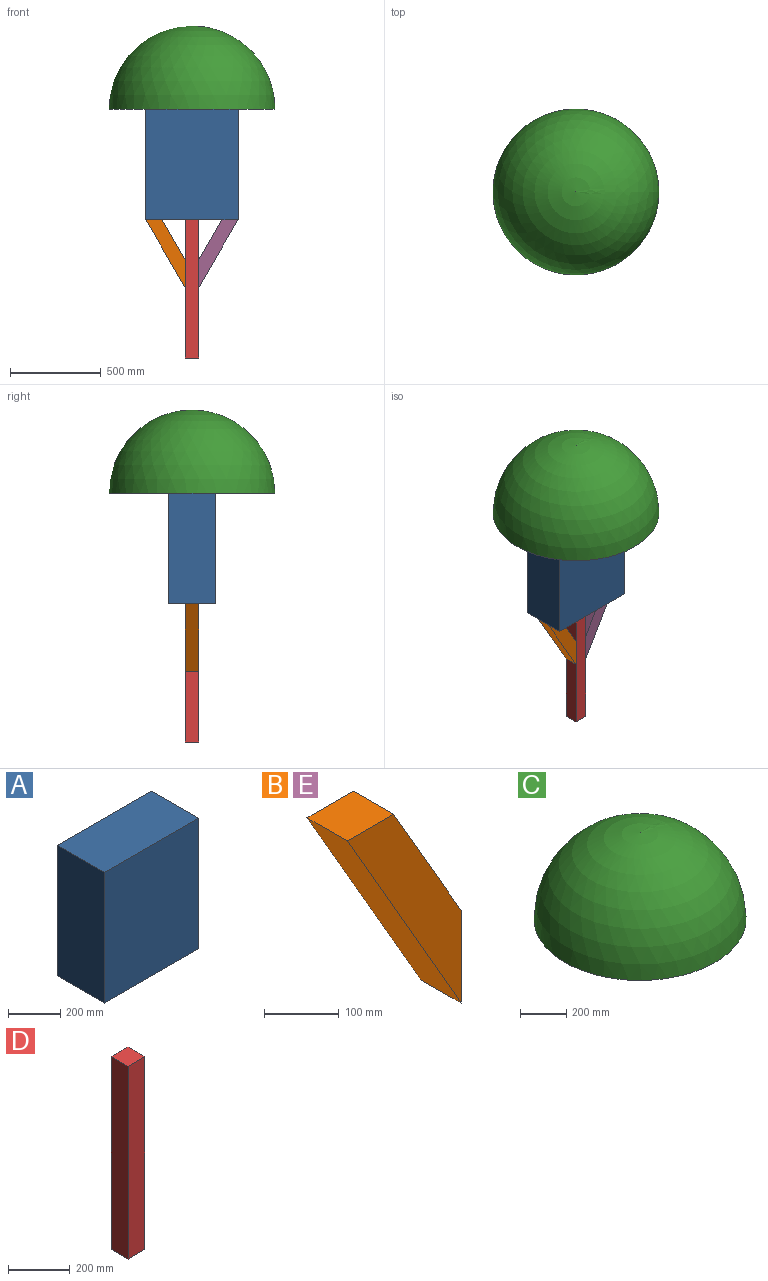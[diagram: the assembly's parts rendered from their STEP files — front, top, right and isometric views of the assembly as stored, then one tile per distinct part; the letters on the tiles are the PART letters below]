
ASSEMBLY  parts=5 mates=4
PART A: 6 faces, bbox 508x254x609.6 mm
  f0: plane 609.6x508mm, normal (0,1,0), area 309676.8mm2, adj f1,f3,f4,f5
  f1: plane 609.6x254mm, normal (-1,0,0), area 154838.4mm2, adj f0,f2,f4,f5
  f2: plane 609.6x508mm, normal (0,-1,0), area 309676.8mm2, adj f1,f3,f4,f5
  f3: plane 609.6x254mm, normal (1,0,0), area 154838.4mm2, adj f0,f2,f4,f5
  f4: plane 508x254mm, normal (0,0,1), area 129032mm2, adj f0,f1,f2,f3
  f5: plane 508x254mm, normal (0,0,-1), area 129032mm2, adj f0,f1,f2,f3
PART B: 6 faces, bbox 215.9x76.2x373.9 mm
  f0: plane 87.99x76.2mm, normal (0,0,1), area 6704.7mm2, adj f1,f3,f4,f5
  f1: plane 373.95x215.9mm, normal (-0.87,0,-0.5), area 32903.2mm2, adj f0,f2,f4,f5
  f2: plane 152.4x76.2mm, normal (1,0,0), area 11612.9mm2, adj f1,f3,f4,f5
  f3: plane 221.55x127.91mm, normal (0.87,0,0.5), area 19493.8mm2, adj f0,f2,f4,f5
  f4: plane 373.95x215.9mm, normal (0,-1,0), area 26198.5mm2, adj f0,f1,f2,f3
  f5: plane 373.95x215.9mm, normal (0,1,0), area 26198.5mm2, adj f0,f1,f2,f3
PART C: 2 faces, bbox 914.4x914.4x457.2 mm
  f0: sphere r=457.2mm, area 1313385.8mm2, adj f1
  f1: plane 914.4x914.4mm, normal (0,0,-1), area 656692.9mm2, adj f0
PART D: 6 faces, bbox 76.2x76.2x762 mm
  f0: plane 76.2x76.2mm, normal (0,0,1), area 5806.4mm2, adj f1,f3,f4,f5
  f1: plane 762x76.2mm, normal (-1,0,0), area 58064.4mm2, adj f0,f2,f4,f5
  f2: plane 76.2x76.2mm, normal (0,0,-1), area 5806.4mm2, adj f1,f3,f4,f5
  f3: plane 762x76.2mm, normal (1,0,0), area 58064.4mm2, adj f0,f2,f4,f5
  f4: plane 762x76.2mm, normal (0,-1,0), area 58064.4mm2, adj f0,f1,f2,f3
  f5: plane 762x76.2mm, normal (0,1,0), area 58064.4mm2, adj f0,f1,f2,f3
PART E: same geometry as B
PLACE A t=(-34.57,-107.52,-436.15)mm
PLACE B t=(-190.92,-69.42,-509.59)mm
PLACE C t=(-34.57,-107.52,-283.75)mm
PLACE D t=(-34.57,-69.42,-817.15)mm
PLACE E rot(axis=(0,0,-1),180deg) t=(121.78,-145.62,-509.59)mm
MATE fastened C.f1 <-> A.f4  axis (0,0,-1) through (-34.57,-107.52,173.45)mm
MATE fastened B.f0 <-> A.f5  axis (0,0,1) through (-288.57,-107.52,-436.15)mm
MATE fastened E.f0 <-> A.f5  axis (0,0,1) through (219.43,-107.52,-436.15)mm
MATE fastened D.f0 <-> A.f5  axis (0,0,1) through (-34.57,-107.52,-436.15)mm
